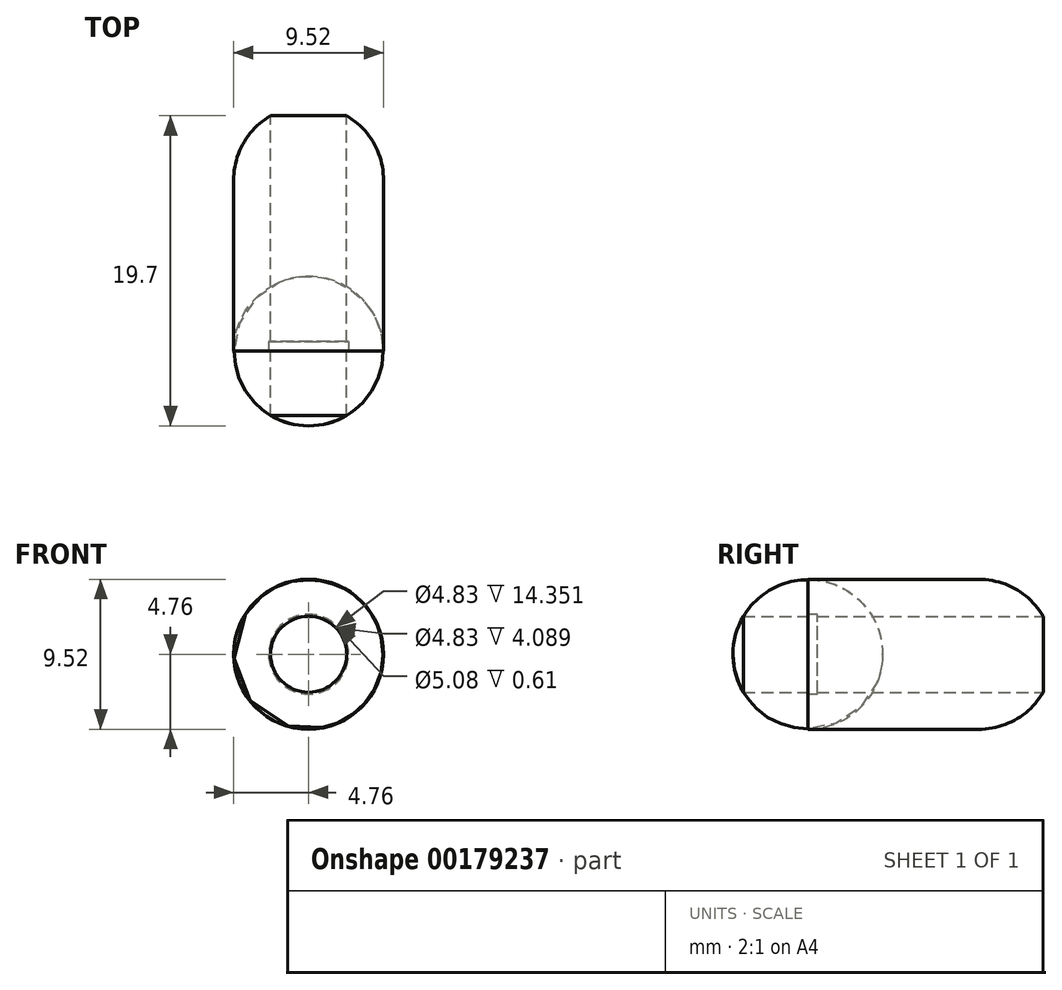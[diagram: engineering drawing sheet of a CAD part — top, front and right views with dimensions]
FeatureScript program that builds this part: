
annotation { "Feature Type Name" : "Feature", "Feature Type Description" : "" }
export const myFeature = defineFeature(function(context is Context, id is Id, definition is map)
    precondition{}
    {
        {
            var Q0;
            Q0=qCreatedBy(makeId("Front.planeOp"),FACE);
            var sketch = newSketch(context, id + "F0", { "sketchPlane" : qUnion([Q0])});
            skCircle(sketch, "E0", {"center": v(0, 0) * mm, "radius": 4.76 * mm});
            skLineSegment(sketch, "E1", {"start": v(0, 0) * mm, "end": v(0, 4.76) * mm, "construction": true});
            skSolve(sketch);
        }
        {
            var Q0;
            Q0=makeQuery(id+"F0.imprint","IMPRINT",FACE,{"disambiguationData":[TD([[makeQuery(id+"F0.imprint","IMPRINT",EDGE,{"derivedFrom":sQuery(id+"F0.wireOp",EDGE,"E0")}),1.0]])]});
            extrude(context, id + "F1", {"entities" : qUnion([Q0]), "depth" : 19.05 * mm});
        }
        {
            var Q0;
            Q0=sQuery(id+"F0.wireOp",EDGE,"E1");
            var Q1;
            Q1=sQuery(id+"F0.wireOp",VERTEX,"E1.end");
            cPlane(context, id + "F2", {"entities" : qUnion([Q0, Q1]), "cplaneType" : CPlaneType.CURVE_POINT, "offset" : 25.4 * mm, "width" : 152.4 * mm, "height" : 152.4 * mm});
        }
        {
            var Q0;
            Q0=makeQuery(id+"F1.opExtrude","CAP_FACE",FACE,{"disambiguationData":[OSD([sQuery(id+"F0.wireOp",EDGE,"E0"),sQuery(id+"F0.wireOp",EDGE,"CJsitaLJ-BcUq-K8IL-UjoE-eBrt7kmqKemN")])],"isStart":false});
            var sketch = newSketch(context, id + "F3", { "sketchPlane" : qUnion([Q0])});
            skLineSegment(sketch, "E2", {"start": v(0, 0) * mm, "end": v(0, 4.76) * mm, "construction": true});
            skSolve(sketch);
        }
        {
            var Q0;
            Q0=makeQuery(id+"F0.imprint","IMPRINT",FACE,{"disambiguationData":[TD([[makeQuery(id+"F0.imprint","IMPRINT",EDGE,{"derivedFrom":sQuery(id+"F0.wireOp",EDGE,"E0")}),1.0]])]});
            var sketch = newSketch(context, id + "F4", { "sketchPlane" : qUnion([Q0])});
            skCircle(sketch, "E3", {"center": v(0, 0) * mm, "radius": 2.41 * mm});
            skSolve(sketch);
        }
        {
            var Q0;
            Q0 = qSketchRegion(id + "F4", true);
            extrude(context, id + "F5", {"entities" : qUnion([Q0]), "operationType" : NewBodyOperationType.REMOVE, "endBound" : BoundingType.THROUGH_ALL, "depth" : 25.4 * mm});
        }
        {
            var Q0;
            Q0=makeQuery(id+"F1.opExtrude","CAP_EDGE",EDGE,{"disambiguationData":[OSD([sQuery(id+"F0.wireOp",EDGE,"E0")])],"isStart":true});
            var Q1;
            Q1=makeQuery(id+"F1.opExtrude","CAP_EDGE",EDGE,{"disambiguationData":[OSD([sQuery(id+"F0.wireOp",EDGE,"E0")])],"isStart":false});
            fillet(context, id + "F6", {"entities" : qUnion([Q0, Q1]), "radius" : 4.75 * mm, "tangentPropagation" : true, "allowEdgeOverflow" : false});
        }
        {
            var Q0;
            Q0=makeQuery(id+"F0.imprint","IMPRINT",FACE,{"disambiguationData":[TD([[makeQuery(id+"F0.imprint","IMPRINT",EDGE,{"derivedFrom":sQuery(id+"F0.wireOp",EDGE,"E0")}),1.0]])]});
            cPlane(context, id + "F7", {"entities" : qUnion([Q0]), "cplaneType" : CPlaneType.OFFSET, "offset" : 14.96 * mm, "width" : 152.4 * mm, "height" : 152.4 * mm});
        }
        {
            var Q0;
            Q0=qCreatedBy(id+"F7.planeOp",FACE);
            var sketch = newSketch(context, id + "F8", { "sketchPlane" : qUnion([Q0])});
            skCircle(sketch, "E4", {"center": v(0, 0) * mm, "radius": 2.54 * mm});
            skSolve(sketch);
        }
        {
            var Q0;
            Q0 = qSketchRegion(id + "F8", true);
            extrude(context, id + "F9", {"entities" : qUnion([Q0]), "operationType" : NewBodyOperationType.REMOVE, "oppositeDirection" : true, "depth" : 0.6 * mm});
        }
    });
